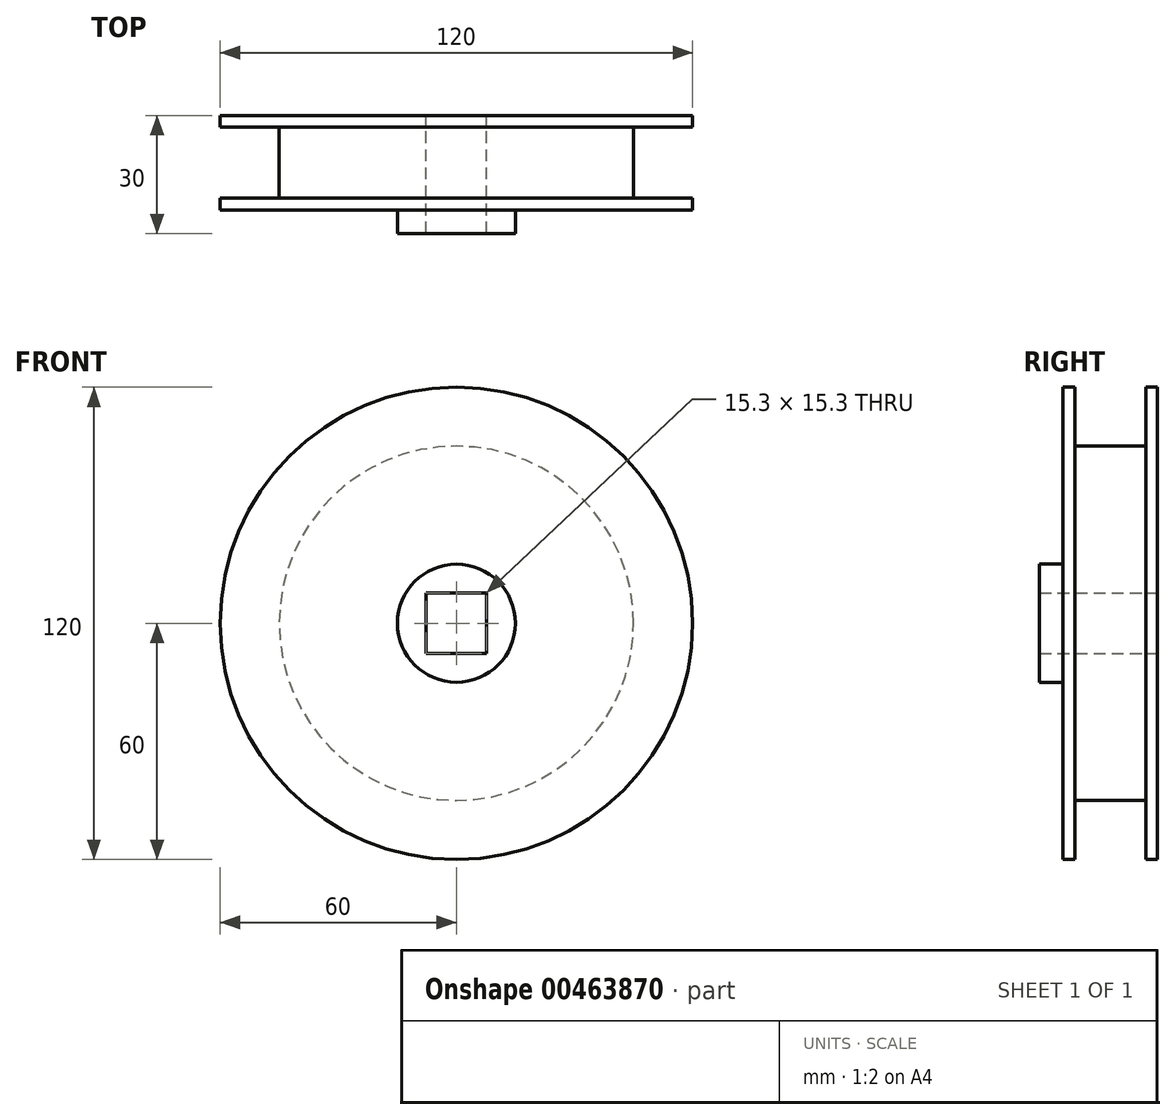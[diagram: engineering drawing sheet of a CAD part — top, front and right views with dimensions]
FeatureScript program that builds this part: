
annotation { "Feature Type Name" : "Feature", "Feature Type Description" : "" }
export const myFeature = defineFeature(function(context is Context, id is Id, definition is map)
    precondition{}
    {
        {
            var Q0;
            Q0=qCreatedBy(makeId("Front.planeOp"),FACE);
            var sketch = newSketch(context, id + "F0", { "sketchPlane" : qUnion([Q0])});
            skCircle(sketch, "E0", {"center": v(0, 0) * mm, "radius": 1.5 * mm});
            skLineSegment(sketch, "E1.bottom", {"start": v(7.5, 7.5) * mm, "end": v(-7.5, 7.5) * mm});
            skLineSegment(sketch, "E1.top", {"start": v(7.5, -7.5) * mm, "end": v(-7.5, -7.5) * mm});
            skLineSegment(sketch, "E1.left", {"start": v(7.5, 7.5) * mm, "end": v(7.5, -7.5) * mm});
            skLineSegment(sketch, "E1.right", {"start": v(-7.5, 7.5) * mm, "end": v(-7.5, -7.5) * mm});
            skSolve(sketch);
        }
        {
            var Q0;
            Q0=makeQuery(id+"F0.imprint","IMPRINT",FACE,{"disambiguationData":[TD([[makeQuery(id+"F0.imprint","IMPRINT",EDGE,{"derivedFrom":sQuery(id+"F0.wireOp",EDGE,"E0")}),-1.0]])]});
            extrude(context, id + "F1", {"entities" : qUnion([Q0]), "depth" : 30 * mm});
        }
        {
            var Q0;
            Q0=makeQuery(id+"F1.opExtrude","SWEPT_FACE",FACE,{"disambiguationData":[OSD([sQuery(id+"F0.wireOp",EDGE,"E1.bottom")])]});
            var sketch = newSketch(context, id + "F2", { "sketchPlane" : qUnion([Q0])});
            skPoint(sketch, "E2", {"position": v(0, -7.42) * mm});
            skPoint(sketch, "E3", {"position": v(0, -23.7) * mm});
            skSolve(sketch);
        }
        {
            var Q0;
            Q0=sQuery(id+"F2.wireOp",VERTEX,"E2");
            var Q1;
            Q1=sQuery(id+"F2.wireOp",VERTEX,"E3");
            var Q2;
            Q2=makeQuery(id+"F1.opExtrude","SWEPT_BODY",BODY,{"disambiguationData":[OSD([sQuery(id+"F0.wireOp",EDGE,"E0"),sQuery(id+"F0.wireOp",EDGE,"E1.bottom"),sQuery(id+"F0.wireOp",EDGE,"E1.top"),sQuery(id+"F0.wireOp",EDGE,"E1.left"),sQuery(id+"F0.wireOp",EDGE,"E1.right")])]});
            hole(context, id + "F3", {"style" : HoleStyle.SIMPLE, "endStyle" : HoleEndStyle.BLIND, "standardTappedOrClearance" : lookupTablePath({ "standard" : "ISO", "fit" : "Normal", "size" : "M3", "type" : "Clearance" }), "standardBlindInLast" : lookupTablePath({ "fit" : "Standard", "standard" : "ISO", "size" : "M3", "type" : "Clearance" }), "holeDiameter" : 3.3 * mm, "holeDepth" : 8 * mm, "isTappedThrough" : true, "tappedDepth" : 12 * mm, "tapClearance" : 3, "startFromSketch" : true, "locations" : qUnion([Q0, Q1]), "scope" : qUnion([Q2])});
        }
        {
            var Q0;
            Q0=qCreatedBy(makeId("Right.planeOp"),FACE);
            var sketch = newSketch(context, id + "F4", { "sketchPlane" : qUnion([Q0])});
            skLineSegment(sketch, "E4", {"start": v(0, 0) * mm, "end": v(0, 60) * mm});
            skLineSegment(sketch, "E5", {"start": v(0, 60) * mm, "end": v(-3, 60) * mm});
            skLineSegment(sketch, "E6", {"start": v(-3, 60) * mm, "end": v(-3, 45) * mm});
            skLineSegment(sketch, "E7", {"start": v(-3, 45) * mm, "end": v(-21, 45) * mm});
            skLineSegment(sketch, "E8", {"start": v(-21, 45) * mm, "end": v(-21, 60) * mm});
            skLineSegment(sketch, "E9", {"start": v(-21, 60) * mm, "end": v(-24, 60) * mm});
            skLineSegment(sketch, "E10", {"start": v(-57.77, 0) * mm, "end": v(8.16, 0) * mm, "construction": true});
            skLineSegment(sketch, "E11", {"start": v(-24, 60) * mm, "end": v(-24, 15) * mm});
            skLineSegment(sketch, "E12", {"start": v(-24, 15) * mm, "end": v(-30, 15) * mm});
            skLineSegment(sketch, "E13", {"start": v(-30, 15) * mm, "end": v(-30, 0) * mm});
            skLineSegment(sketch, "E14", {"start": v(-30, 0) * mm, "end": v(0, 0) * mm});
            skSolve(sketch);
        }
        {
            var Q0;
            Q0=makeQuery(id+"F4.imprint","IMPRINT",FACE,{"disambiguationData":[TD([[makeQuery(id+"F4.imprint","IMPRINT",EDGE,{"derivedFrom":sQuery(id+"F4.wireOp",EDGE,"E4")}),1.0]])]});
            var Q1;
            Q1=sQuery(id+"F4.wireOp",EDGE,"E10");
            revolve(context, id + "F5", {"entities" : qUnion([Q0]), "axis" : qUnion([Q1]), "revolveType" : RevolveType.FULL});
        }
        {
            var Q0;
            Q0=qCreatedBy(makeId("Front.planeOp"),FACE);
            var sketch = newSketch(context, id + "F6", { "sketchPlane" : qUnion([Q0])});
            skPoint(sketch, "E15.middle", {"position": v(0, 0) * mm});
            skLineSegment(sketch, "E16.bottom", {"start": v(-7.65, 7.65) * mm, "end": v(7.65, 7.65) * mm});
            skLineSegment(sketch, "E16.top", {"start": v(-7.65, -7.65) * mm, "end": v(7.65, -7.65) * mm});
            skLineSegment(sketch, "E16.left", {"start": v(-7.65, 7.65) * mm, "end": v(-7.65, -7.65) * mm});
            skLineSegment(sketch, "E16.right", {"start": v(7.65, 7.65) * mm, "end": v(7.65, -7.65) * mm});
            skSolve(sketch);
        }
        {
            var Q0;
            Q0=makeQuery(id+"F6.imprint","IMPRINT",FACE,{"disambiguationData":[TD([[makeQuery(id+"F6.imprint","IMPRINT",EDGE,{"derivedFrom":sQuery(id+"F6.wireOp",EDGE,"E16.bottom")}),-1.0]])]});
            var Q1;
            Q1=makeQuery(id+"F5.opRevolve","SWEPT_FACE",FACE,{"disambiguationData":[OSD([sQuery(id+"F4.wireOp",EDGE,"Ak5UeXPM-1aMY-JCr2-oYsb-4lNAeW0wst2F")])]});
            extrude(context, id + "F7", {"entities" : qUnion([Q0]), "operationType" : NewBodyOperationType.REMOVE, "endBound" : BoundingType.THROUGH_ALL, "endBoundEntityFace" : qUnion([Q1]), "depth" : 25 * mm});
        }
    });
